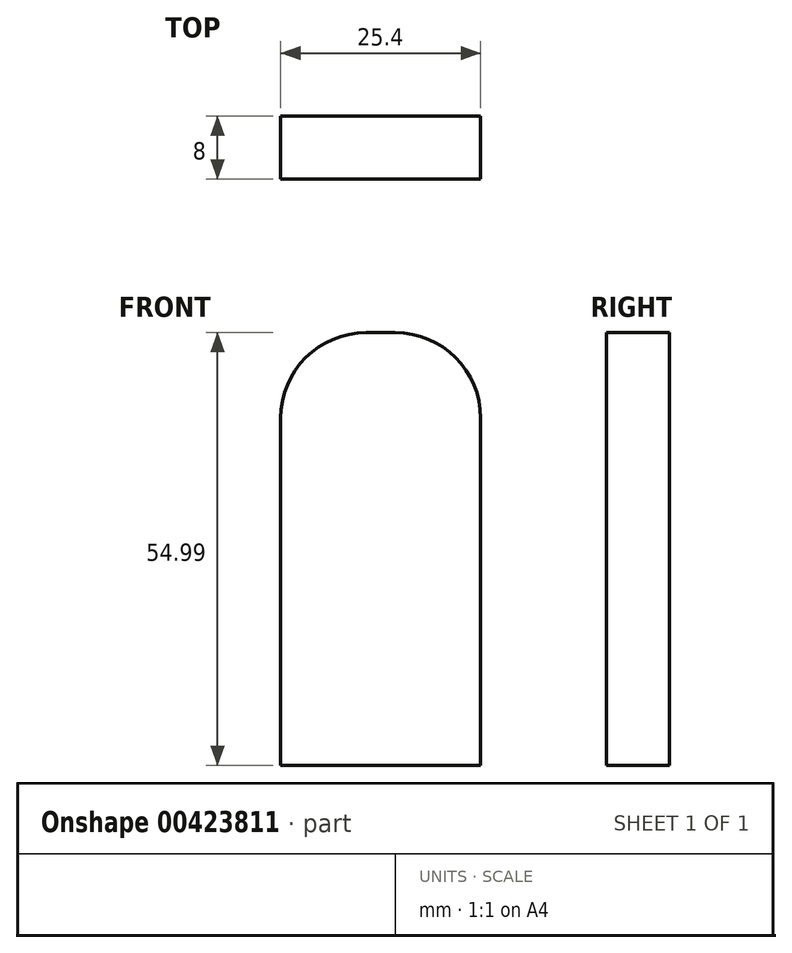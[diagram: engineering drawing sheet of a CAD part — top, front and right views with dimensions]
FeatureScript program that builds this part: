
annotation { "Feature Type Name" : "Feature", "Feature Type Description" : "" }
export const myFeature = defineFeature(function(context is Context, id is Id, definition is map)
    precondition{}
    {
        {
            var Q0;
            Q0=qCreatedBy(makeId("Front.planeOp"),FACE);
            var sketch = newSketch(context, id + "F0", { "sketchPlane" : qUnion([Q0])});
            skLineSegment(sketch, "E0.bottom", {"start": v(0, 0) * mm, "end": v(-25.4, 0) * mm});
            skLineSegment(sketch, "E0.top", {"start": v(-10.87, 55) * mm, "end": v(-14.53, 55) * mm});
            skLineSegment(sketch, "E0.left", {"start": v(0, 0) * mm, "end": v(0, 44.12) * mm});
            skLineSegment(sketch, "E0.right", {"start": v(-25.4, 0) * mm, "end": v(-25.4, 44.12) * mm});
            skPoint(sketch, "E1.visualSharp", {"position": v(-25.4, 55) * mm});
            skArc(sketch, "E1.filletArc", {"start": v(-14.53, 55) * mm, "mid": v(-22.22, 51.8) * mm, "end": v(-25.4, 44.12) * mm});
            skPoint(sketch, "E2.visualSharp", {"position": v(0, 55) * mm});
            skArc(sketch, "E2.filletArc", {"start": v(0, 44.12) * mm, "mid": v(-3.18, 51.8) * mm, "end": v(-10.87, 55) * mm});
            skSolve(sketch);
        }
        {
            var Q0;
            Q0 = qSketchRegion(id + "F0", true);
            extrude(context, id + "F1", {"entities" : qUnion([Q0]), "depth" : 8 * mm});
        }
    });
